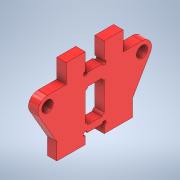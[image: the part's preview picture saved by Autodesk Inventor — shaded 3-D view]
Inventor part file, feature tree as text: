
AUTODESK INVENTOR PART (.ipt)
format: ipt  version: 2021 (Build 250183000, 183)  size: 157,184 bytes
history: native  units: in
note: dims shown in document units (in); Inventor stores cm internally (conversion verified against a paired STEP export)
features: sketch x2, extrude x1
ambient origin geometry x8: Origin, YZ Plane, XZ Plane, XY Plane, X Axis, Y Axis, Z Axis, Center Point
bodies: Solid1 (feature_tree)
feature tree (3):
  sketch  "Sketch1"  dims[d21=1.378in d22=2.1654in]
  sketch  "Sketch2"  dims[d23=3.3465in d24=0.4724in d25=0.0984in d26=0.7874in d27=3.1496in d28=0.7874in d29=3.937in d30=0.3937in d31=0.0in d32=30.0deg]
  extrude  "Extrusion1"  Depth=2.1654in
